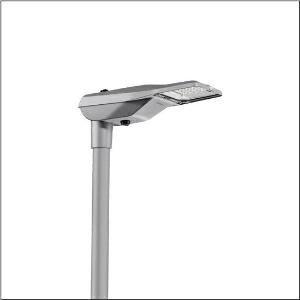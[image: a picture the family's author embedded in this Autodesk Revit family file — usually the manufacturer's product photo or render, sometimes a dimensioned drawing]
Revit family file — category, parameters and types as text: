
# Revit family: streetlight_sl_21_iq_micro___stw1_0a_5xe1e31y08cb_f1b3
name_source: partatom
category: Lighting Fixtures
units: mm (PartAtom-declared; Revit-internal decimal feet)

## family parameters
Cut with Voids When Loaded = No
Host = Face
Light Source = No
Part Type = Normal
Room Calculation Point = No
Round Connector Dimension = Use Diameter
Shared = No

## types (1)
- --- (1 x LED, 2880 lm, 19.1 W, 3000K)
    Apparent Load = 19 VA
    CIE Flux Codes = 38 75 98 100 100
    Color Rendering = 70
    Color Temperature = 3000K
    Default Elevation = 1800 mm
    Description = Streetlight SL 21 iQ micro, mast luminaire, primary light control with lens, of PMMA, primary optical cover: cover, of toughened safety glass, transparent, light distribution: STW1.0a, light emission: direct distribution, primary light characteristic: asymmetric, installation type: post-top, side-entry, LED, High Power LED, rated luminous flux: 2.880lm, luminous efficacy: 151lm/W, light colour: 730, colour temperature: 3000K, control: presetting dimming logarithmic, Street-Remote, Auto-Match, Temp-Guard, Lumen-Switch, Night-Set, Smart-Wire, Light-Fading, Desk-Remote (wireless, voltage-free reading and setting of iQ features in the workshop via application-optimized NFC function/RFID function), optimised constant luminous flux control (CLO 2.0), mains connection: 220..240V, AC, 50/60Hz, start of lifetime: 19W, end of service life: 20W, reduction: 9W, luminaire housing, of diecast aluminium, powder-coated, Siteco® metallic grey (DB 702S), corrosivity category C5 mid according to DIN EN ISO 12944, please order mast flange separately, inclination adjustable: 0°, 5°, 10°, 15°, sealing non-destructively replaceable, multi-level sealing system, length: 528mm, width: 235mm, height: 110mm, mast flange for spigot size: 42mm (side-entry): 5XC10008XM4, 60/48mm (side-entry/post-top): 5XC10108XM2, 76/60mm (side-entry/post-top): 5XC10108XM1, Smart Interface below and above, protection rating (complete): IP66, insulation class (complete): insulation class II (safety insulation), certification: CE, ENEC, ENEC+, VDE, impact resistance: IK09, permissible operating ambient temperature for outdoor applications: -40..+50°C, standard-compliant lighting for roads and squares, packaging unit: 1 piece

Light Distribution: STW1.0a
    Height = 110 mm
    Lamp = 1 x LED
    Lamp Light Flux = 2880 lm
    Lamp Power = 19.1 W
    Lamp count = 1
    Length = 528 mm
    Luminous efficacy = 151 lm/W
    Manufacturer = Siteco
    ModVariant = No
    Model = 5XE1E31Y08CB
    Number of Poles = 1
    OnlyDefault = Yes
    Power Factor = 1
    Product Name = Streetlight SL 21 iQ micro | STW1.0a
    Product group = mast luminaire | pylon top
    ProductGroupID = 6100
    Protection Class = Protection class II
    Protection Degree = IP 66
    RLX_Detail_Level = 1
    RLX_Emergency_Light_Flux = 0 lm
    RLX_Emergency_Type = 0
    RLX_Emergency_Type_DB = No
    RlxData = <blob elided: 99425 chars, md5=7db1d0da>
    Socket = socket
    Standby Power = 0 W
    System Light Flux = 2880 lm
    System Power = 19 W
    Type Comments = factory setting: luminous flux: 100 % | dim-lin: 254 | 387 mA
    Type Image = l_1007239.jpg
    URL = http://relux.com
    VarID = @adj_044455
    Voltage = 0 V
    Weight = 0.00 kg
    Width = 235 mm

## geometry (parser evidence)
native form markers: Blend x4, Sweep x9
no freeform markers — native parametric forms only
